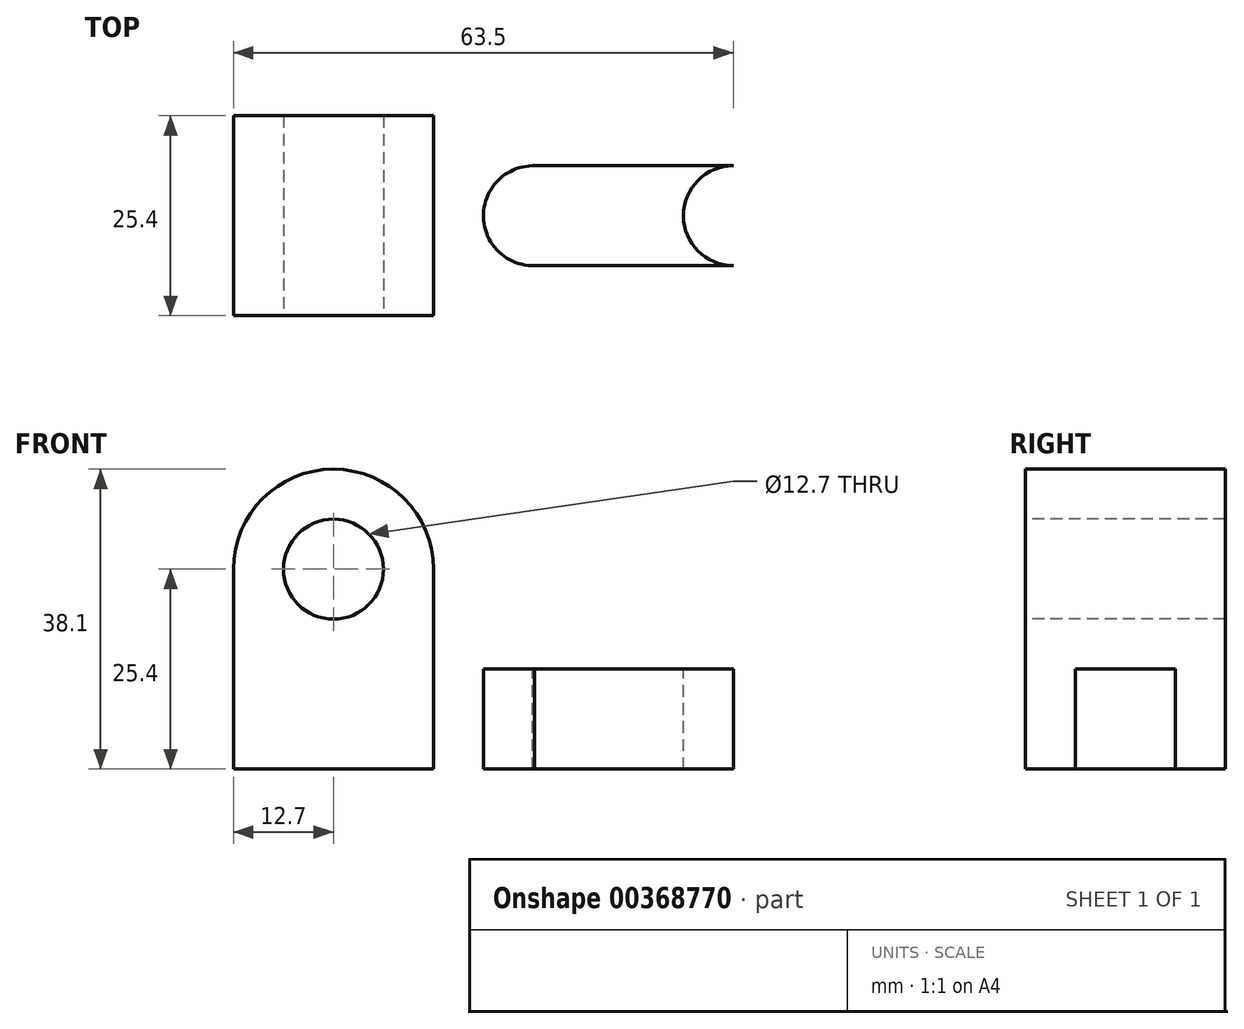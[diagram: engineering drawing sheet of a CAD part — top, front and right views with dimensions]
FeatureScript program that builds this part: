
annotation { "Feature Type Name" : "Feature", "Feature Type Description" : "" }
export const myFeature = defineFeature(function(context is Context, id is Id, definition is map)
    precondition{}
    {
        {
            var Q0;
            Q0=qCreatedBy(makeId("Front.planeOp"),FACE);
            var sketch = newSketch(context, id + "F0", { "sketchPlane" : qUnion([Q0])});
            skLineSegment(sketch, "E0", {"start": v(0, 0) * mm, "end": v(0, 25.4) * mm});
            skLineSegment(sketch, "E1", {"start": v(25.4, 25.4) * mm, "end": v(25.4, 0) * mm});
            skLineSegment(sketch, "E2", {"start": v(25.4, 0) * mm, "end": v(0, 0) * mm});
            skArc(sketch, "E3", {"start": v(25.4, 25.4) * mm, "mid": v(12.7, 38.1) * mm, "end": v(0, 25.4) * mm});
            skCircle(sketch, "E4", {"center": v(12.7, 25.4) * mm, "radius": 6.35 * mm});
            skSolve(sketch);
        }
        {
            var Q0;
            Q0=makeQuery(id+"F0.imprint","IMPRINT",FACE,{"disambiguationData":[TD([[makeQuery(id+"F0.imprint","IMPRINT",EDGE,{"derivedFrom":sQuery(id+"F0.wireOp",EDGE,"E0")}),-1.0]])]});
            var sketch = newSketch(context, id + "F1", { "sketchPlane" : qUnion([Q0])});
            skSolve(sketch);
        }
        {
            var Q0;
            Q0 = qSketchRegion(id + "F1", true);
            var Q1;
            Q1=makeQuery(id+"F0.imprint","IMPRINT",FACE,{"disambiguationData":[TD([[makeQuery(id+"F0.imprint","IMPRINT",EDGE,{"derivedFrom":sQuery(id+"F0.wireOp",EDGE,"E0")}),-1.0]])]});
            extrude(context, id + "F2", {"entities" : qUnion([Q0, Q1]), "oppositeDirection" : true, "depth" : 25.4 * mm});
        }
        {
            var Q0;
            Q0=makeQuery(id+"F2.opExtrude","SWEPT_FACE",FACE,{"disambiguationData":[OSD([sQuery(id+"F0.wireOp",EDGE,"E1")])]});
            var sketch = newSketch(context, id + "F3", { "sketchPlane" : qUnion([Q0])});
            skLineSegment(sketch, "E5", {"start": v(0, 0) * mm, "end": v(0, 12.7) * mm});
            skLineSegment(sketch, "E6", {"start": v(0, 12.7) * mm, "end": v(25.4, 12.7) * mm});
            skLineSegment(sketch, "E7", {"start": v(25.4, 12.7) * mm, "end": v(25.4, 0) * mm});
            skLineSegment(sketch, "E8", {"start": v(25.4, 0) * mm, "end": v(0, 0) * mm});
            skSolve(sketch);
        }
        {
            var Q0;
            Q0=makeQuery(id+"F3.imprint","IMPRINT",FACE,{"disambiguationData":[TD([[makeQuery(id+"F3.imprint","IMPRINT",EDGE,{"derivedFrom":sQuery(id+"F3.wireOp",EDGE,"E5")}),1.0]])]});
            extrude(context, id + "F4", {"entities" : qUnion([Q0]), "operationType" : NewBodyOperationType.ADD, "depth" : 50.8 * mm});
        }
        {
            var Q0;
            Q0=makeQuery(id+"F4.opExtrude","CAP_EDGE",EDGE,{"disambiguationData":[OSD([sQuery(id+"F3.wireOp",EDGE,"E5")])],"isStart":false});
            var Q1;
            Q1=makeQuery(id+"F4.opExtrude","CAP_EDGE",EDGE,{"disambiguationData":[OSD([sQuery(id+"F3.wireOp",EDGE,"E7")])],"isStart":false});
            fillet(context, id + "F5", {"entities" : qUnion([Q0, Q1]), "radius" : 12.7 * mm, "tangentPropagation" : true, "allowEdgeOverflow" : false});
        }
        {
            var Q0;
            Q0=makeQuery(id+"F4.opExtrude","SWEPT_FACE",FACE,{"disambiguationData":[OSD([sQuery(id+"F3.wireOp",EDGE,"E6")])]});
            var sketch = newSketch(context, id + "F6", { "sketchPlane" : qUnion([Q0])});
            skCircle(sketch, "E9", {"center": v(38.1, 12.7) * mm, "radius": 6.35 * mm});
            skCircle(sketch, "E10", {"center": v(63.5, 12.7) * mm, "radius": 6.35 * mm});
            skLineSegment(sketch, "E11", {"start": v(37.96, 19.05) * mm, "end": v(63.5, 19.05) * mm});
            skLineSegment(sketch, "E12", {"start": v(37.95, 6.35) * mm, "end": v(63.5, 6.35) * mm});
            skPoint(sketch, "E13.orphan", {"position": v(25.4, 12.7) * mm});
            skPoint(sketch, "E14.start.orphan", {"position": v(76.2, 12.7) * mm});
            skSolve(sketch);
        }
        {
            var Q0;
            {var subQ0=sQuery(id+"F6.wireOp",EDGE,"E11");var subQ1=sQuery(id+"F6.wireOp",EDGE,"E9");var subQ2=makeQuery(id+"F6.imprint","INTERSECT",VERTEX,{"disambiguationData":[OD(0.0)],"derivedFrom":[subQ1,subQ0]});Q0=makeQuery(id+"F6.imprint","IMPRINT",FACE,{"disambiguationData":[TD([[makeQuery(id+"F6.imprint","IMPRINT",EDGE,{"disambiguationData":[TD([[subQ2,-1.0]])],"derivedFrom":subQ1}),1.0]])]});}
            var Q1;
            {var subQ0=sQuery(id+"F6.wireOp",EDGE,"E11");var subQ1=sQuery(id+"F6.wireOp",EDGE,"E9");var subQ2=makeQuery(id+"F6.imprint","INTERSECT",VERTEX,{"disambiguationData":[OD(1.0)],"derivedFrom":[subQ1,subQ0]});Q1=makeQuery(id+"F6.imprint","IMPRINT",FACE,{"disambiguationData":[TD([[makeQuery(id+"F6.imprint","IMPRINT",EDGE,{"disambiguationData":[TD([[subQ2,1.0]])],"derivedFrom":subQ1}),-1.0]])]});}
            var Q2;
            {var subQ0=sQuery(id+"F6.wireOp",EDGE,"E10");var subQ1=makeQuery(id+"F6.imprint","INTERSECT",VERTEX,{"derivedFrom":[subQ0,sQuery(id+"F6.wireOp",EDGE,"E11")]});Q2=makeQuery(id+"F6.imprint","IMPRINT",FACE,{"disambiguationData":[TD([[makeQuery(id+"F6.imprint","IMPRINT",EDGE,{"disambiguationData":[TD([[subQ1,-1.0]])],"derivedFrom":subQ0}),1.0]])]});}
            extrude(context, id + "F7", {"entities" : qUnion([Q0, Q1, Q2]), "operationType" : NewBodyOperationType.REMOVE, "oppositeDirection" : true, "depth" : 25.4 * mm});
        }
    });
